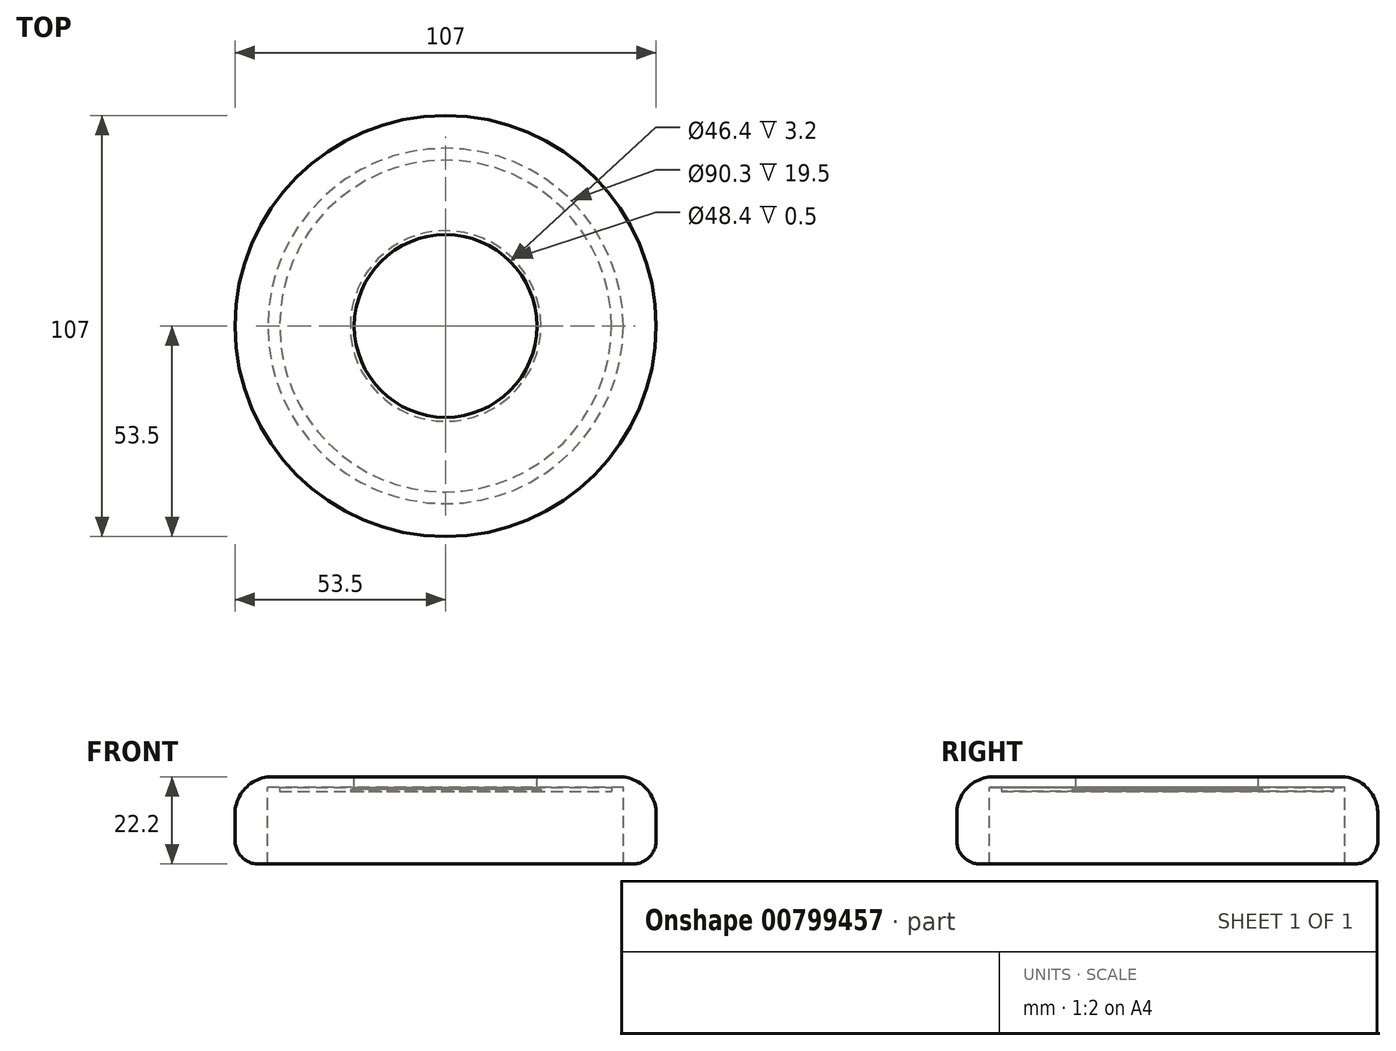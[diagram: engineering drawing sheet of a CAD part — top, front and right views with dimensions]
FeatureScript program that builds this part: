
annotation { "Feature Type Name" : "Feature", "Feature Type Description" : "" }
export const myFeature = defineFeature(function(context is Context, id is Id, definition is map)
    precondition{}
    {
        {
            var Q0;
            Q0=qCreatedBy(makeId("Front.planeOp"),FACE);
            var sketch = newSketch(context, id + "F0", { "sketchPlane" : qUnion([Q0])});
            skLineSegment(sketch, "E0", {"start": v(0, 0) * mm, "end": v(45.15, 0) * mm, "construction": true});
            skLineSegment(sketch, "E1", {"start": v(45.15, 18.5) * mm, "end": v(0, 18.5) * mm, "construction": true});
            skLineSegment(sketch, "E2", {"start": v(0, 18.5) * mm, "end": v(0, 0) * mm, "construction": true});
            skLineSegment(sketch, "E3", {"start": v(23.2, 42.79) * mm, "end": v(23.2, -26.94) * mm, "construction": true});
            skLineSegment(sketch, "E4", {"start": v(53.5, 44.25) * mm, "end": v(53.5, -26.7) * mm, "construction": true});
            skLineSegment(sketch, "E5", {"start": v(-22.8, 22.2) * mm, "end": v(106.9, 22.2) * mm, "construction": true});
            skLineSegment(sketch, "E6", {"start": v(0, 72.78) * mm, "end": v(0, -65.95) * mm, "construction": true});
            skLineSegment(sketch, "E7", {"start": v(23.2, 22.2) * mm, "end": v(53.5, 22.2) * mm});
            skLineSegment(sketch, "E8", {"start": v(53.5, 22.2) * mm, "end": v(53.5, 0) * mm});
            skLineSegment(sketch, "E9", {"start": v(53.5, 0) * mm, "end": v(45.15, 0) * mm});
            skLineSegment(sketch, "E10", {"start": v(45.15, 18.5) * mm, "end": v(23.2, 18.5) * mm});
            skLineSegment(sketch, "E11", {"start": v(23.2, 18.5) * mm, "end": v(23.2, 22.2) * mm});
            skLineSegment(sketch, "E12", {"start": v(45.15, 18.5) * mm, "end": v(45.15, 0) * mm});
            skSolve(sketch);
        }
        {
            var Q0;
            Q0 = qSketchRegion(id + "F0", true);
            var Q1;
            Q1=sQuery(id+"F0.wireOp",EDGE,"E6");
            revolve(context, id + "F1", {"surfaceOperationType" : NewSurfaceOperationType.NEW, "entities" : qUnion([Q0]), "axis" : qUnion([Q1]), "revolveType" : RevolveType.FULL});
        }
        {
            var Q0;
            Q0=makeQuery(id+"F1.opRevolve","SWEPT_EDGE",EDGE,{"disambiguationData":[OSD([sQuery(id+"F0.wireOp",EDGE,"E7"),sQuery(id+"F0.wireOp",EDGE,"E8")])]});
            fillet(context, id + "F2", {"entities" : qUnion([Q0]), "radius" : 9.5 * mm, "tangentPropagation" : true, "allowEdgeOverflow" : false});
        }
        {
            var Q0;
            Q0=makeQuery(id+"F1.opRevolve","SWEPT_EDGE",EDGE,{"disambiguationData":[OSD([sQuery(id+"F0.wireOp",EDGE,"E8"),sQuery(id+"F0.wireOp",EDGE,"E9")])]});
            fillet(context, id + "F3", {"entities" : qUnion([Q0]), "radius" : 6 * mm, "tangentPropagation" : true, "allowEdgeOverflow" : false});
        }
        {
            var Q0;
            Q0=makeQuery(id+"F1.opRevolve","SWEPT_FACE",FACE,{"disambiguationData":[OSD([sQuery(id+"F0.wireOp",EDGE,"E10")])]});
            var sketch = newSketch(context, id + "F4", { "sketchPlane" : qUnion([Q0])});
            skCircle(sketch, "E13", {"center": v(0, 0) * mm, "radius": 42.15 * mm});
            skCircle(sketch, "E14", {"center": v(0, 0) * mm, "radius": 24.2 * mm});
            skSolve(sketch);
        }
        {
            var Q0;
            Q0=makeQuery(id+"F4.imprint","IMPRINT",FACE,{"disambiguationData":[TD([[makeQuery(id+"F4.imprint","IMPRINT",EDGE,{"derivedFrom":sQuery(id+"F4.wireOp",EDGE,"E13")}),-1.0]])]});
            extrude(context, id + "F5", {"entities" : qUnion([Q0]), "operationType" : NewBodyOperationType.REMOVE, "oppositeDirection" : true, "depth" : 1 * mm, "offsetDistance" : 25 * mm});
        }
        {
            var Q0;
            Q0=makeQuery(id+"F4.imprint","IMPRINT",FACE,{"disambiguationData":[TD([[makeQuery(id+"F4.imprint","IMPRINT",EDGE,{"derivedFrom":sQuery(id+"F4.wireOp",EDGE,"E14")}),1.0]])]});
            extrude(context, id + "F6", {"entities" : qUnion([Q0]), "operationType" : NewBodyOperationType.REMOVE, "oppositeDirection" : true, "depth" : 0.5 * mm, "offsetDistance" : 25 * mm});
        }
    });
